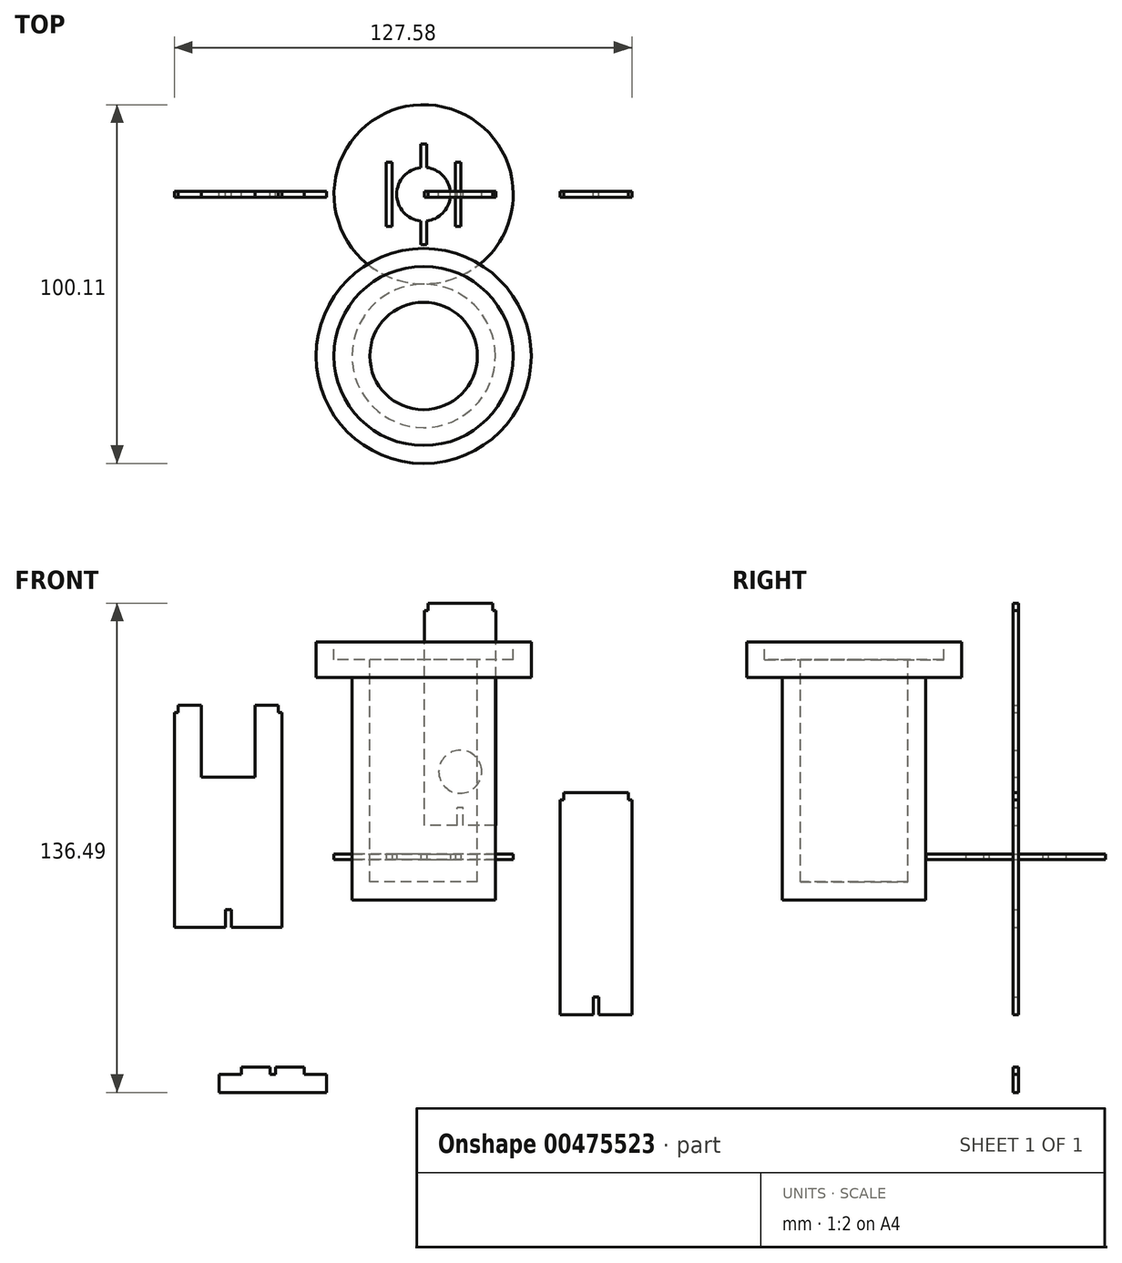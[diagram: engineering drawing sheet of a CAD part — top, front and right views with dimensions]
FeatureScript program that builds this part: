
annotation { "Feature Type Name" : "Feature", "Feature Type Description" : "" }
export const myFeature = defineFeature(function(context is Context, id is Id, definition is map)
    precondition{}
    {
        {
            var Q0;
            Q0=qCreatedBy(makeId("Top.planeOp"),FACE);
            var sketch = newSketch(context, id + "F0", { "sketchPlane" : qUnion([Q0])});
            skCircle(sketch, "E0", {"center": v(0, 0) * mm, "radius": 25 * mm});
            skCircle(sketch, "E1", {"center": v(0, 0) * mm, "radius": 7.5 * mm});
            skLineSegment(sketch, "E2.bottom", {"start": v(0.8, -14) * mm, "end": v(-0.8, -14) * mm});
            skLineSegment(sketch, "E2.top", {"start": v(0.8, 14) * mm, "end": v(-0.8, 14) * mm});
            skLineSegment(sketch, "E2.left", {"start": v(0.8, -14) * mm, "end": v(0.8, 14) * mm});
            skLineSegment(sketch, "E2.right", {"start": v(-0.8, -14) * mm, "end": v(-0.8, 14) * mm});
            skLineSegment(sketch, "E3.bottom", {"start": v(-8.8, -9) * mm, "end": v(-10.4, -9) * mm});
            skLineSegment(sketch, "E3.top", {"start": v(-8.8, 9) * mm, "end": v(-10.4, 9) * mm});
            skLineSegment(sketch, "E3.left", {"start": v(-8.8, -9) * mm, "end": v(-8.8, 9) * mm});
            skLineSegment(sketch, "E3.right", {"start": v(-10.4, -9) * mm, "end": v(-10.4, 9) * mm});
            skPoint(sketch, "E3.middle", {"position": v(-9.6, 0) * mm});
            skCircle(sketch, "E4", {"center": v(0, 0) * mm, "radius": 15 * mm, "construction": true});
            skLineSegment(sketch, "E5.bottom", {"start": v(10.4, -9) * mm, "end": v(8.8, -9) * mm});
            skLineSegment(sketch, "E5.top", {"start": v(10.4, 9) * mm, "end": v(8.8, 9) * mm});
            skLineSegment(sketch, "E5.left", {"start": v(10.4, -9) * mm, "end": v(10.4, 9) * mm});
            skLineSegment(sketch, "E5.right", {"start": v(8.8, -9) * mm, "end": v(8.8, 9) * mm});
            skPoint(sketch, "E5.middle", {"position": v(9.6, 0) * mm});
            skSolve(sketch);
        }
        {
            var Q0;
            Q0=makeQuery(id+"F0.imprint","IMPRINT",FACE,{"disambiguationData":[TD([[makeQuery(id+"F0.imprint","IMPRINT",EDGE,{"derivedFrom":sQuery(id+"F0.wireOp",EDGE,"E0")}),1.0]])]});
            extrude(context, id + "F1", {"entities" : qUnion([Q0]), "depth" : 1.6 * mm});
        }
        {
            var Q0;
            Q0=qCreatedBy(makeId("Front.planeOp"),FACE);
            var sketch = newSketch(context, id + "F2", { "sketchPlane" : qUnion([Q0])});
            skLineSegment(sketch, "E6.bottom", {"start": v(-68.5, 43.04) * mm, "end": v(-62, 43.04) * mm});
            skLineSegment(sketch, "E6.top", {"start": v(-69.5, -18.96) * mm, "end": v(-55.3, -18.96) * mm});
            skLineSegment(sketch, "E6.left", {"start": v(-69.5, 41.04) * mm, "end": v(-69.5, -18.96) * mm});
            skLineSegment(sketch, "E6.right", {"start": v(-39.5, 41.04) * mm, "end": v(-39.5, -18.96) * mm});
            skLineSegment(sketch, "E7.top", {"start": v(-62, 23.04) * mm, "end": v(-47, 23.04) * mm});
            skLineSegment(sketch, "E7.left", {"start": v(-62, 43.04) * mm, "end": v(-62, 23.04) * mm});
            skLineSegment(sketch, "E7.right", {"start": v(-47, 43.04) * mm, "end": v(-47, 23.04) * mm});
            skLineSegment(sketch, "E8.trimOffspring", {"start": v(-47, 43.04) * mm, "end": v(-40.5, 43.04) * mm});
            skLineSegment(sketch, "E9", {"start": v(-54.5, -18.96) * mm, "end": v(-54.5, 23.04) * mm, "construction": true});
            skPoint(sketch, "E9.endSnap0", {"position": v(-54.5, 23.04) * mm});
            skLineSegment(sketch, "E10", {"start": v(-54.5, 23.04) * mm, "end": v(-54.5, 43.04) * mm, "construction": true});
            skLineSegment(sketch, "E11", {"start": v(-62, 43.04) * mm, "end": v(-54.5, 43.04) * mm, "construction": true});
            skLineSegment(sketch, "E12", {"start": v(-54.5, 43.04) * mm, "end": v(-47, 43.04) * mm, "construction": true});
            skLineSegment(sketch, "E13.top", {"start": v(-69.5, 41.04) * mm, "end": v(-68.5, 41.04) * mm});
            skLineSegment(sketch, "E13.right", {"start": v(-68.5, 43.04) * mm, "end": v(-68.5, 41.04) * mm});
            skLineSegment(sketch, "E14.top", {"start": v(-39.5, 41.04) * mm, "end": v(-40.5, 41.04) * mm});
            skLineSegment(sketch, "E14.right", {"start": v(-40.5, 43.04) * mm, "end": v(-40.5, 41.04) * mm});
            skLineSegment(sketch, "E15", {"start": v(-68.5, 41.04) * mm, "end": v(-40.5, 41.04) * mm, "construction": true});
            skLineSegment(sketch, "E16.top", {"start": v(-53.7, -13.96) * mm, "end": v(-55.3, -13.96) * mm});
            skLineSegment(sketch, "E16.left", {"start": v(-53.7, -18.96) * mm, "end": v(-53.7, -13.96) * mm});
            skLineSegment(sketch, "E16.right", {"start": v(-55.3, -18.96) * mm, "end": v(-55.3, -13.96) * mm});
            skPoint(sketch, "E16.middle", {"position": v(-54.5, -16.46) * mm});
            skLineSegment(sketch, "E17.trimOffspring", {"start": v(-53.7, -18.96) * mm, "end": v(-39.5, -18.96) * mm});
            skSolve(sketch);
        }
        {
            var Q0;
            Q0 = qSketchRegion(id + "F2", true);
            extrude(context, id + "F3", {"entities" : qUnion([Q0]), "endBound" : BoundingType.SYMMETRIC, "depth" : 1.6 * mm});
        }
        {
            var Q0;
            Q0=qCreatedBy(makeId("Front.planeOp"),FACE);
            var sketch = newSketch(context, id + "F4", { "sketchPlane" : qUnion([Q0])});
            skLineSegment(sketch, "E18.bottom", {"start": v(57.08, 18.7) * mm, "end": v(39.08, 18.7) * mm});
            skLineSegment(sketch, "E18.top", {"start": v(58.08, -43.3) * mm, "end": v(48.88, -43.3) * mm});
            skLineSegment(sketch, "E18.left", {"start": v(58.08, 16.7) * mm, "end": v(58.08, -43.3) * mm});
            skLineSegment(sketch, "E18.right", {"start": v(38.08, 16.7) * mm, "end": v(38.08, -43.3) * mm});
            skPoint(sketch, "E18.middle", {"position": v(48.08, -12.3) * mm});
            skLineSegment(sketch, "E19.top", {"start": v(38.08, 16.7) * mm, "end": v(39.08, 16.7) * mm});
            skLineSegment(sketch, "E19.right", {"start": v(39.08, 18.7) * mm, "end": v(39.08, 16.7) * mm});
            skLineSegment(sketch, "E20.top", {"start": v(58.08, 16.7) * mm, "end": v(57.08, 16.7) * mm});
            skLineSegment(sketch, "E20.right", {"start": v(57.08, 18.7) * mm, "end": v(57.08, 16.7) * mm});
            skLineSegment(sketch, "E21", {"start": v(39.08, 16.7) * mm, "end": v(57.08, 16.7) * mm, "construction": true});
            skPoint(sketch, "E22.orphan", {"position": v(38.08, 18.7) * mm});
            skPoint(sketch, "E23.orphan", {"position": v(58.08, 18.7) * mm});
            skLineSegment(sketch, "E24", {"start": v(48.08, -43.3) * mm, "end": v(48.08, 18.7) * mm, "construction": true});
            skLineSegment(sketch, "E25.top", {"start": v(48.88, -38.3) * mm, "end": v(47.28, -38.3) * mm});
            skLineSegment(sketch, "E25.left", {"start": v(48.88, -43.3) * mm, "end": v(48.88, -38.3) * mm});
            skLineSegment(sketch, "E25.right", {"start": v(47.28, -43.3) * mm, "end": v(47.28, -38.3) * mm});
            skPoint(sketch, "E25.middle", {"position": v(48.08, -40.8) * mm});
            skLineSegment(sketch, "E26.trimOffspring", {"start": v(47.28, -43.3) * mm, "end": v(38.08, -43.3) * mm});
            skSolve(sketch);
        }
        {
            var Q0;
            Q0 = qSketchRegion(id + "F4", true);
            extrude(context, id + "F5", {"entities" : qUnion([Q0]), "endBound" : BoundingType.SYMMETRIC, "depth" : 1.6 * mm});
        }
        {
            var Q0;
            Q0=qCreatedBy(makeId("Front.planeOp"),FACE);
            var sketch = newSketch(context, id + "F6", { "sketchPlane" : qUnion([Q0])});
            skLineSegment(sketch, "E27.bottom", {"start": v(20.2, 9.53) * mm, "end": v(11, 9.53) * mm});
            skLineSegment(sketch, "E27.top", {"start": v(19.2, 71.53) * mm, "end": v(1.2, 71.53) * mm});
            skLineSegment(sketch, "E27.left", {"start": v(20.2, 9.53) * mm, "end": v(20.2, 69.53) * mm});
            skLineSegment(sketch, "E27.right", {"start": v(0.2, 9.53) * mm, "end": v(0.2, 69.53) * mm});
            skPoint(sketch, "E27.middle", {"position": v(10.2, 40.53) * mm});
            skLineSegment(sketch, "E28.top", {"start": v(0.2, 69.53) * mm, "end": v(1.2, 69.53) * mm});
            skLineSegment(sketch, "E28.right", {"start": v(1.2, 71.53) * mm, "end": v(1.2, 69.53) * mm});
            skLineSegment(sketch, "E29.top", {"start": v(20.2, 69.53) * mm, "end": v(19.2, 69.53) * mm});
            skLineSegment(sketch, "E29.right", {"start": v(19.2, 71.53) * mm, "end": v(19.2, 69.53) * mm});
            skLineSegment(sketch, "E30", {"start": v(10.2, 71.53) * mm, "end": v(10.2, 9.53) * mm, "construction": true});
            skCircle(sketch, "E31", {"center": v(10.2, 24.53) * mm, "radius": 6 * mm});
            skLineSegment(sketch, "E32", {"start": v(1.2, 69.53) * mm, "end": v(19.2, 69.53) * mm, "construction": true});
            skPoint(sketch, "E33.orphan", {"position": v(0.2, 71.53) * mm});
            skPoint(sketch, "E34.orphan", {"position": v(20.2, 71.53) * mm});
            skLineSegment(sketch, "E35.top", {"start": v(11, 14.53) * mm, "end": v(9.4, 14.53) * mm});
            skLineSegment(sketch, "E35.left", {"start": v(11, 9.53) * mm, "end": v(11, 14.53) * mm});
            skLineSegment(sketch, "E35.right", {"start": v(9.4, 9.53) * mm, "end": v(9.4, 14.53) * mm});
            skPoint(sketch, "E35.middle", {"position": v(10.2, 12.03) * mm});
            skLineSegment(sketch, "E36.trimOffspring", {"start": v(9.4, 9.53) * mm, "end": v(0.2, 9.53) * mm});
            skSolve(sketch);
        }
        {
            var Q0;
            Q0=makeQuery(id+"F6.imprint","IMPRINT",FACE,{"disambiguationData":[TD([[makeQuery(id+"F6.imprint","IMPRINT",EDGE,{"derivedFrom":sQuery(id+"F6.wireOp",EDGE,"E27.bottom")}),-1.0]])]});
            extrude(context, id + "F7", {"entities" : qUnion([Q0]), "endBound" : BoundingType.SYMMETRIC, "depth" : 1.6 * mm});
        }
        {
            var Q0;
            Q0=qCreatedBy(makeId("Front.planeOp"),FACE);
            var sketch = newSketch(context, id + "F8", { "sketchPlane" : qUnion([Q0])});
            skLineSegment(sketch, "E37", {"start": v(-57.06, -64.96) * mm, "end": v(-27.06, -64.96) * mm});
            skLineSegment(sketch, "E38", {"start": v(-27.06, -64.96) * mm, "end": v(-27.06, -59.96) * mm});
            skLineSegment(sketch, "E39", {"start": v(-27.06, -59.96) * mm, "end": v(-33.26, -59.96) * mm});
            skLineSegment(sketch, "E40", {"start": v(-33.26, -59.96) * mm, "end": v(-33.26, -57.96) * mm});
            skLineSegment(sketch, "E41", {"start": v(-33.26, -57.96) * mm, "end": v(-41.26, -57.96) * mm});
            skLineSegment(sketch, "E42", {"start": v(-41.26, -57.96) * mm, "end": v(-41.26, -59.96) * mm});
            skLineSegment(sketch, "E43", {"start": v(-41.26, -59.96) * mm, "end": v(-42.86, -59.96) * mm});
            skLineSegment(sketch, "E44", {"start": v(-42.86, -59.96) * mm, "end": v(-42.86, -57.96) * mm});
            skLineSegment(sketch, "E45", {"start": v(-42.86, -57.96) * mm, "end": v(-50.86, -57.96) * mm});
            skLineSegment(sketch, "E46", {"start": v(-50.86, -57.96) * mm, "end": v(-50.86, -59.96) * mm});
            skLineSegment(sketch, "E47", {"start": v(-50.86, -59.96) * mm, "end": v(-57.06, -59.96) * mm});
            skLineSegment(sketch, "E48", {"start": v(-57.06, -59.96) * mm, "end": v(-57.06, -64.96) * mm});
            skLineSegment(sketch, "E49", {"start": v(-50.86, -59.96) * mm, "end": v(-42.86, -59.96) * mm, "construction": true});
            skLineSegment(sketch, "E50", {"start": v(-41.26, -59.96) * mm, "end": v(-33.26, -59.96) * mm, "construction": true});
            skLineSegment(sketch, "E51", {"start": v(-42.06, -59.96) * mm, "end": v(-42.06, -64.96) * mm, "construction": true});
            skLineSegment(sketch, "E52", {"start": v(-42.86, -57.96) * mm, "end": v(-41.26, -57.96) * mm, "construction": true});
            skSolve(sketch);
        }
        {
            var Q0;
            Q0=makeQuery(id+"F8.imprint","IMPRINT",FACE,{"disambiguationData":[TD([[makeQuery(id+"F8.imprint","IMPRINT",EDGE,{"derivedFrom":sQuery(id+"F8.wireOp",EDGE,"E37")}),1.0]])]});
            extrude(context, id + "F9", {"entities" : qUnion([Q0]), "endBound" : BoundingType.SYMMETRIC, "depth" : 1.6 * mm});
        }
        {
            var Q0;
            Q0=qCreatedBy(makeId("Right.planeOp"),FACE);
            var sketch = newSketch(context, id + "F10", { "sketchPlane" : qUnion([Q0])});
            skLineSegment(sketch, "E53", {"start": v(-45.11, 82.48) * mm, "end": v(-45.11, -6.25) * mm, "construction": true});
            skLineSegment(sketch, "E54", {"start": v(-45.11, -6.25) * mm, "end": v(-45.11, -11.25) * mm});
            skLineSegment(sketch, "E55", {"start": v(-45.11, -11.25) * mm, "end": v(-65.11, -11.25) * mm});
            skLineSegment(sketch, "E56", {"start": v(-65.11, -11.25) * mm, "end": v(-65.11, 50.75) * mm});
            skLineSegment(sketch, "E57", {"start": v(-65.11, 50.75) * mm, "end": v(-75.11, 50.75) * mm});
            skLineSegment(sketch, "E58", {"start": v(-75.11, 50.75) * mm, "end": v(-75.11, 60.75) * mm});
            skLineSegment(sketch, "E59", {"start": v(-75.11, 60.75) * mm, "end": v(-70.11, 60.75) * mm});
            skLineSegment(sketch, "E60", {"start": v(-70.11, 60.75) * mm, "end": v(-70.11, 55.75) * mm});
            skLineSegment(sketch, "E61", {"start": v(-70.11, 55.75) * mm, "end": v(-60.11, 55.75) * mm});
            skLineSegment(sketch, "E62", {"start": v(-60.11, 55.75) * mm, "end": v(-60.11, -6.25) * mm});
            skLineSegment(sketch, "E63", {"start": v(-60.11, -6.25) * mm, "end": v(-45.11, -6.25) * mm});
            skSolve(sketch);
        }
        {
            var Q0;
            Q0 = qSketchRegion(id + "F10", true);
            var Q1;
            Q1=sQuery(id+"F10.wireOp",EDGE,"E54");
            revolve(context, id + "F11", {"entities" : qUnion([Q0]), "axis" : qUnion([Q1]), "revolveType" : RevolveType.FULL});
        }
    });
